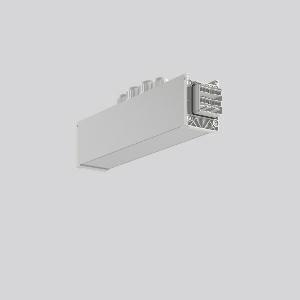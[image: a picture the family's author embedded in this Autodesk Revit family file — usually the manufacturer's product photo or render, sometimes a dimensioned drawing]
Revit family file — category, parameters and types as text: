
# Revit family: linedo_mitteleinspeisung_7pol_982698_000_3_9687
name_source: partatom
category: Lighting Fixtures
units: mm (PartAtom-declared; Revit-internal decimal feet)

## family parameters
Cut with Voids When Loaded = No
Host = Face
Light Source = No
Part Type = Normal
Room Calculation Point = No
Round Connector Dimension = Use Diameter
Shared = No

## types (1)
- LINEDO_Mitteleinspeisung_7pol
    Apparent Load = 0 VA
    Default Elevation = 1800 mm
    Description = Series: LINEDO
Middle power feed, 7-pole, connection socket / plug. Housing: extruded aluminium profile, anodised. Cover made of plastic, surface like housing. LINEDO plug system, plastic, light grey. 4 cable glands (2 x M20 and 2 x M25). Cable glands on top. Easy connection for rigid or flexible wires.
Colour: anodised aluminium
Length: 330 mm
Width: 58 mm
Height: 76 mm
Weight: 751 g
    Height = 76 mm
    Lamp = 0 x
    Length = 330 mm
    Luminous efficacy = 0 lm/W
    Manufacturer = RZB
    ModVariant = No
    Model = 982698.000.3
    Mounting Place = Ceiling
    Mounting Type = Surface mounted, Pendant
    Number of Poles = 1
    OnlyDefault = Yes
    Power Factor = 1
    Product Name = LINEDO_Mitteleinspeisung_7pol
    Product group = Surface mounted continuous line luminaire system
    ProductGroupID = 310
    Protection Class = Protection class I
    Protection Degree = IP 54
    RLX_Detail_Level = 1
    RLX_Emergency_Light_Flux = 0 lm
    RLX_Emergency_Type = 0
    RLX_Emergency_Type_DB = No
    RlxData = <blob elided: 21869 chars, md5=5ee0252b>
    Standby Power = 0 W
    System Light Flux = 0 lm
    System Power = 0 W
    Type Comments = Product without accessories
    Type Image = 982698.000.jpg
    URL = http://relux.com
    VarID = ---
    Voltage = 0 V
    Weight = 0.00 kg
    Width = 58 mm

## geometry (parser evidence)
native form markers: Blend x4, Sweep x10
no freeform markers — native parametric forms only
